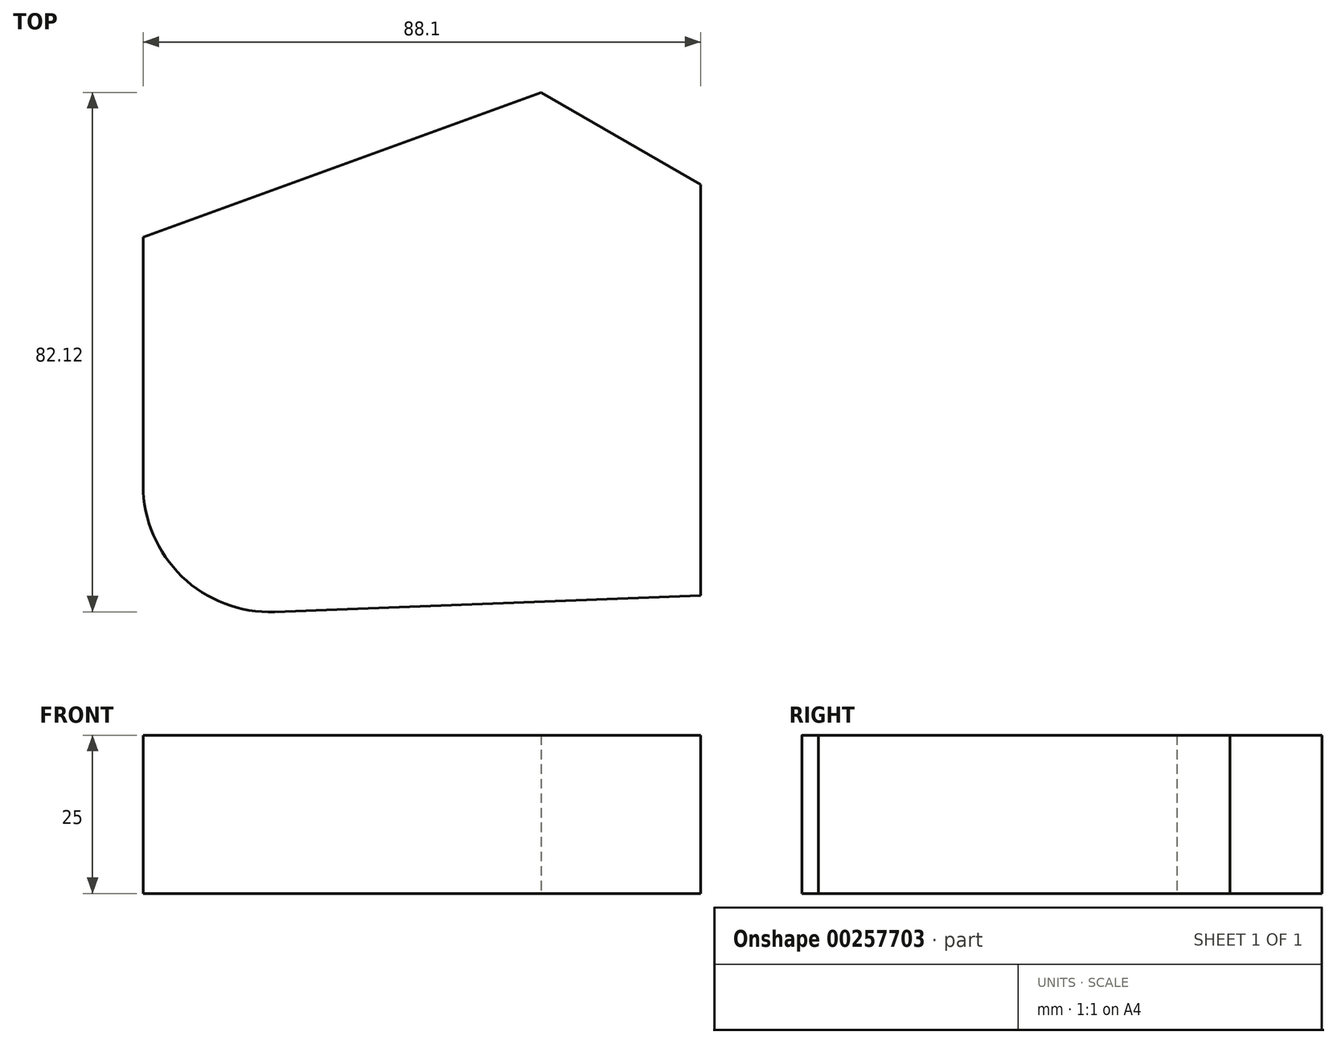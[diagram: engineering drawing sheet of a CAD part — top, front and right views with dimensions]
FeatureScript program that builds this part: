
annotation { "Feature Type Name" : "Feature", "Feature Type Description" : "" }
export const myFeature = defineFeature(function(context is Context, id is Id, definition is map)
    precondition{}
    {
        {
            var Q0;
            Q0=qCreatedBy(makeId("Top.planeOp"),FACE);
            var sketch = newSketch(context, id + "F0", { "sketchPlane" : qUnion([Q0])});
            skLineSegment(sketch, "E0", {"start": v(-68.01, 36.13) * mm, "end": v(-68.01, -3.1) * mm});
            skLineSegment(sketch, "E1", {"start": v(-68.01, 36.13) * mm, "end": v(-5.11, 59.02) * mm});
            skLineSegment(sketch, "E2", {"start": v(-5.11, 59.02) * mm, "end": v(20.09, 44.48) * mm});
            skLineSegment(sketch, "E3", {"start": v(20.09, 44.48) * mm, "end": v(20.09, -20.52) * mm});
            skLineSegment(sketch, "E4", {"start": v(-68.01, 36.13) * mm, "end": v(-48.24, 36.13) * mm});
            skLineSegment(sketch, "E5", {"start": v(20.09, 44.48) * mm, "end": v(-4.83, 44.48) * mm});
            skLineSegment(sketch, "E6", {"start": v(20.09, -20.52) * mm, "end": v(-47.25, -23.08) * mm});
            skPoint(sketch, "E7.visualSharp", {"position": v(-68.01, -23.87) * mm});
            skArc(sketch, "E7.filletArc", {"start": v(-68.01, -3.1) * mm, "mid": v(-61.89, -17.5) * mm, "end": v(-47.25, -23.08) * mm});
            skSolve(sketch);
        }
        {
            var Q0;
            Q0 = qSketchRegion(id + "F0", true);
            extrude(context, id + "F1", {"entities" : qUnion([Q0]), "depth" : 25 * mm});
        }
    });
